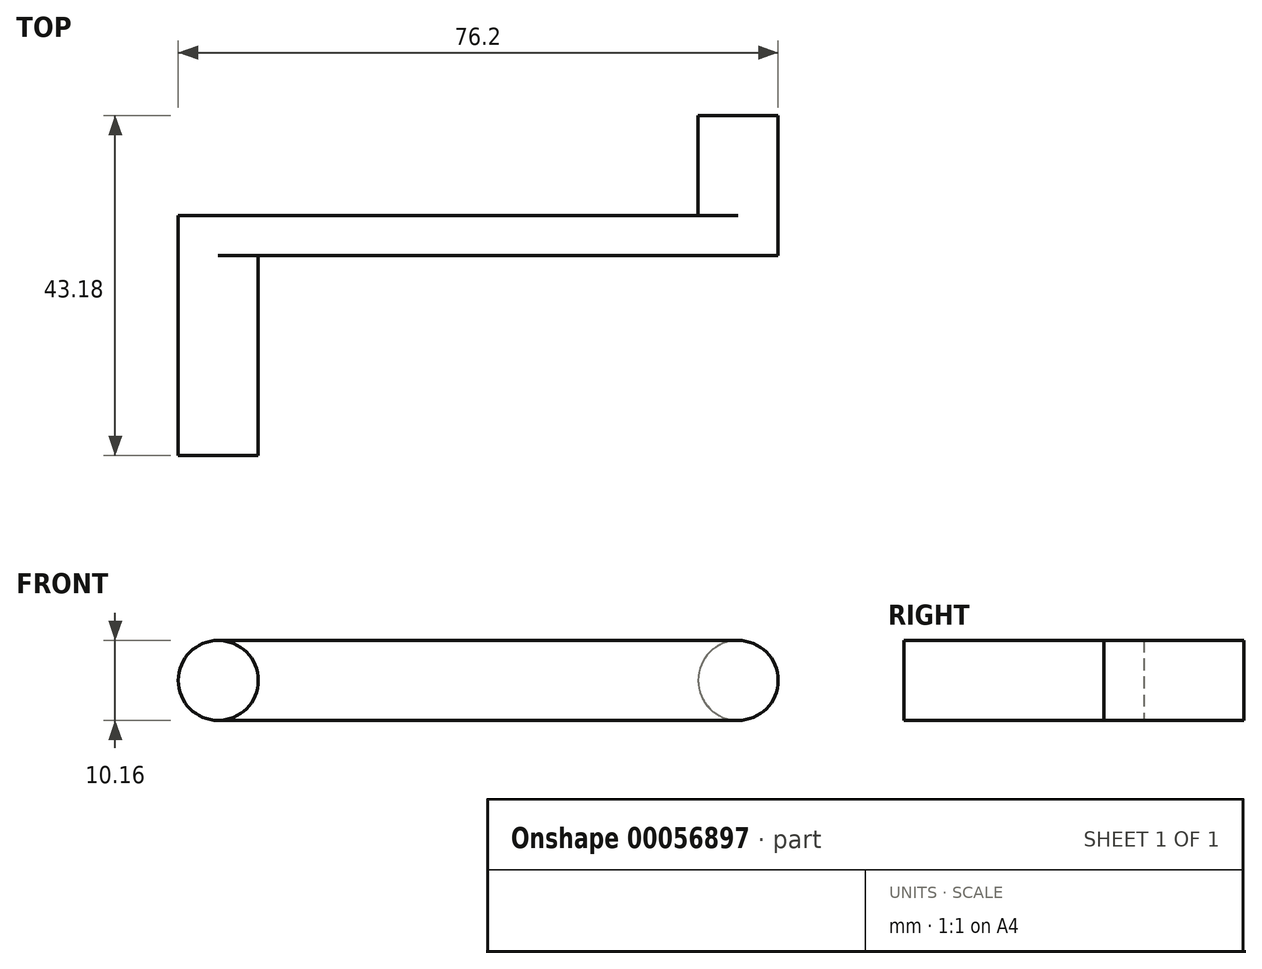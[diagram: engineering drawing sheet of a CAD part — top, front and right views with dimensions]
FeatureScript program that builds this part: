
annotation { "Feature Type Name" : "Feature", "Feature Type Description" : "" }
export const myFeature = defineFeature(function(context is Context, id is Id, definition is map)
    precondition{}
    {
        {
            var Q0;
            Q0=qCreatedBy(makeId("Front.planeOp"),FACE);
            var sketch = newSketch(context, id + "F0", { "sketchPlane" : qUnion([Q0])});
            skLineSegment(sketch, "E0.rect.bottom", {"start": v(-38.1, 5.08) * mm, "end": v(38.1, 5.08) * mm});
            skLineSegment(sketch, "E0.rect.top", {"start": v(-38.1, -5.08) * mm, "end": v(38.1, -5.08) * mm});
            skLineSegment(sketch, "E0.rect.left", {"start": v(-38.1, 5.08) * mm, "end": v(-38.1, -5.08) * mm});
            skLineSegment(sketch, "E0.rect.right", {"start": v(38.1, 5.08) * mm, "end": v(38.1, -5.08) * mm});
            skPoint(sketch, "E0.rect.middle", {"position": v(0, 0) * mm});
            skLineSegment(sketch, "E1", {"start": v(-38.1, 0) * mm, "end": v(-33.02, 0) * mm});
            skLineSegment(sketch, "E2", {"start": v(38.1, 0) * mm, "end": v(33.02, 0) * mm});
            skPoint(sketch, "E3", {"position": v(-33.02, 0) * mm});
            skPoint(sketch, "E4", {"position": v(33.02, 0) * mm});
            skCircle(sketch, "E5", {"center": v(-33.02, 0) * mm, "radius": 5.08 * mm});
            skCircle(sketch, "E6", {"center": v(33.02, 0) * mm, "radius": 5.08 * mm});
            skSolve(sketch);
        }
        {
            var Q0;
            {var subQ0=sQuery(id+"F0.wireOp",EDGE,"E5");var subQ1=makeQuery(id+"F0.imprint","INTERSECT",VERTEX,{"derivedFrom":[sQuery(id+"F0.wireOp",EDGE,"E0.rect.left"),subQ0]});Q0=makeQuery(id+"F0.imprint","IMPRINT",FACE,{"disambiguationData":[TD([[makeQuery(id+"F0.imprint","IMPRINT",EDGE,{"disambiguationData":[TD([[subQ1,1.0]])],"derivedFrom":subQ0}),1.0]])]});}
            var Q1;
            {var subQ0=sQuery(id+"F0.wireOp",EDGE,"E5");var subQ1=sQuery(id+"F0.wireOp",EDGE,"E0.rect.bottom");var subQ2=makeQuery(id+"F0.imprint","INTERSECT",VERTEX,{"derivedFrom":[subQ1,subQ0]});Q1=makeQuery(id+"F0.imprint","IMPRINT",FACE,{"disambiguationData":[TD([[makeQuery(id+"F0.imprint","IMPRINT",EDGE,{"disambiguationData":[TD([[subQ2,-1.0]])],"derivedFrom":subQ1}),-1.0]])]});}
            var Q2;
            {var subQ0=sQuery(id+"F0.wireOp",EDGE,"E6");var subQ1=makeQuery(id+"F0.imprint","INTERSECT",VERTEX,{"derivedFrom":[sQuery(id+"F0.wireOp",EDGE,"E0.rect.right"),subQ0]});Q2=makeQuery(id+"F0.imprint","IMPRINT",FACE,{"disambiguationData":[TD([[makeQuery(id+"F0.imprint","IMPRINT",EDGE,{"disambiguationData":[TD([[subQ1,-1.0]])],"derivedFrom":subQ0}),1.0]])]});}
            extrude(context, id + "F1", {"entities" : qUnion([Q0, Q1, Q2]), "oppositeDirection" : true, "depth" : 5.08 * mm});
        }
        {
            var Q0;
            {var subQ0=sQuery(id+"F0.wireOp",EDGE,"E5");var subQ1=makeQuery(id+"F0.imprint","INTERSECT",VERTEX,{"derivedFrom":[sQuery(id+"F0.wireOp",EDGE,"E0.rect.left"),subQ0]});Q0=makeQuery(id+"F0.imprint","IMPRINT",FACE,{"disambiguationData":[TD([[makeQuery(id+"F0.imprint","IMPRINT",EDGE,{"disambiguationData":[TD([[subQ1,1.0]])],"derivedFrom":subQ0}),1.0]])]});}
            extrude(context, id + "F2", {"entities" : qUnion([Q0]), "operationType" : NewBodyOperationType.ADD, "depth" : 25.4 * mm});
        }
        {
            var Q0;
            {var subQ0=sQuery(id+"F0.wireOp",EDGE,"E6");var subQ1=makeQuery(id+"F0.imprint","INTERSECT",VERTEX,{"derivedFrom":[sQuery(id+"F0.wireOp",EDGE,"E0.rect.right"),subQ0]});Q0=makeQuery(id+"F0.imprint","IMPRINT",FACE,{"disambiguationData":[TD([[makeQuery(id+"F0.imprint","IMPRINT",EDGE,{"disambiguationData":[TD([[subQ1,-1.0]])],"derivedFrom":subQ0}),1.0]])]});}
            extrude(context, id + "F3", {"entities" : qUnion([Q0]), "operationType" : NewBodyOperationType.ADD, "oppositeDirection" : true, "depth" : 17.78 * mm});
        }
    });
